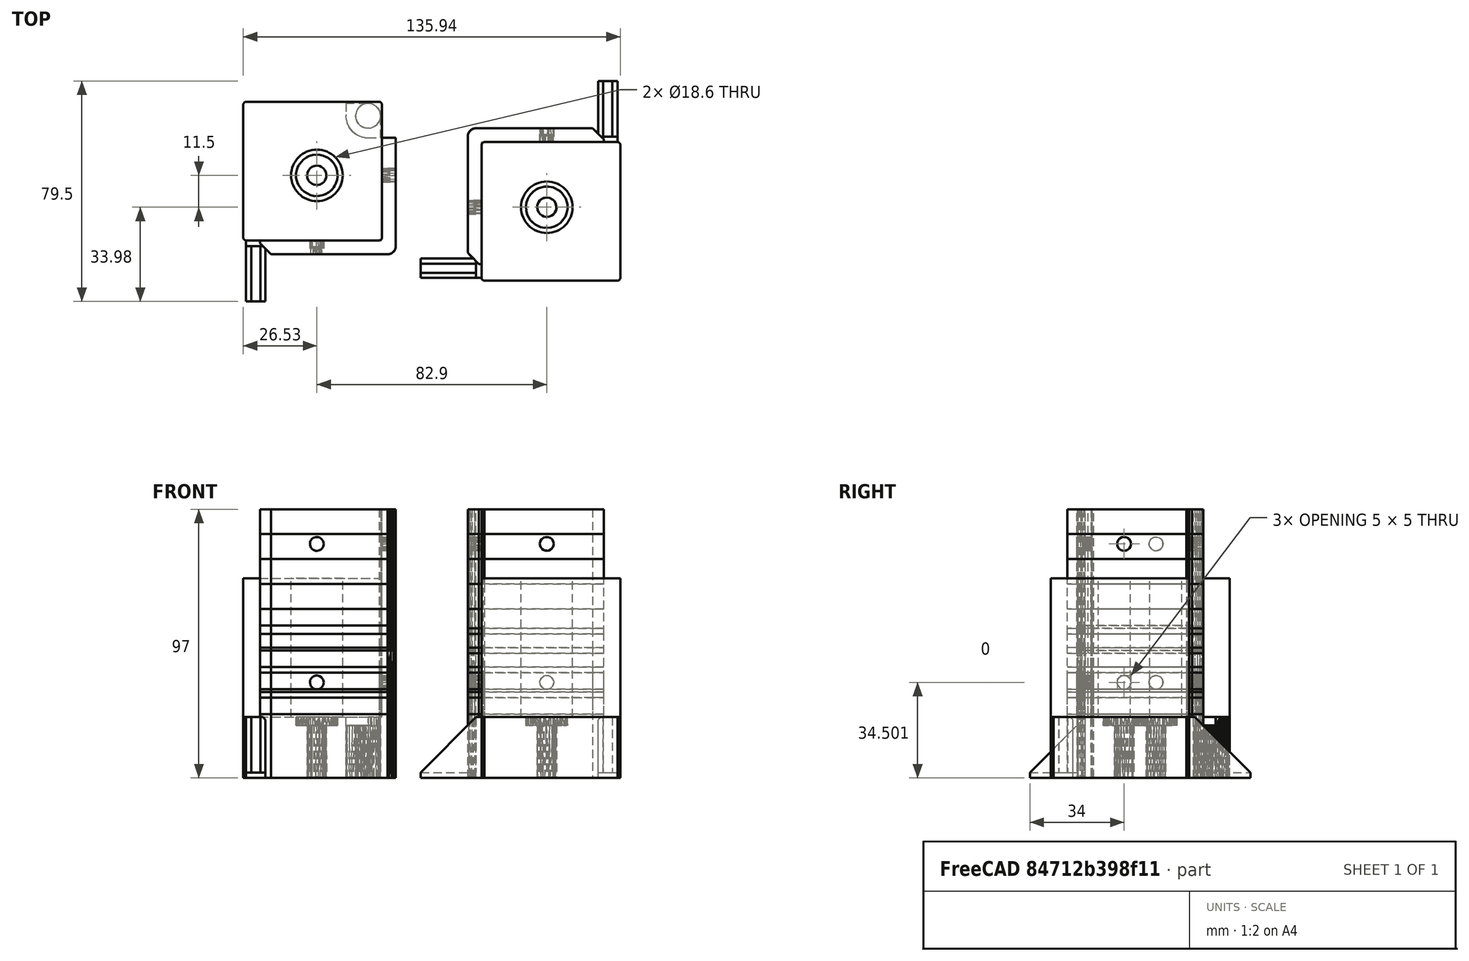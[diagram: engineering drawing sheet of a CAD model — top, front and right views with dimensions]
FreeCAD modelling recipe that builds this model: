
FCSTD DOCUMENT  (FreeCAD 0.18R14555 (Git shallow))
Label: top-holder-50mm-extend
License: All rights reserved
LicenseURL: http://en.wikipedia.org/wiki/All_rights_reserved
objects: Part::Feature×22, Part::Box×7, Part::Cut×5, Part::MultiCommon×4, Part::Cylinder×2, App::DocumentObjectGroup×2, Part::Fillet×1
note: 41 computed .brp shape members not serialized (recipe doc carries the construction recipe); baked Part::Feature solids carry a one-line shape summary decoded from their .brp

FEATURE [Part::Feature] top_corner_handle001001_solid  label="top_corner_handle002 (Solid)"
  Placement = pos=(30.38,0.35,0) rot=(0,0,1;0rad)
  shape: bbox 55 x 72 x 47 mm, 346 faces (baked)
FEATURE [Part::Feature] blain_top_corner001001_solid  label="blain_top_corner002 (Solid)"
  Placement = pos=(52.59,0.98,0) rot=(0,0,1;0rad)
  shape: bbox 72 x 72 x 47 mm, 277 faces (baked)
FEATURE [Part::Box] Box  label="Cube"
  AttacherType = Attacher::AttachEngine3D
  Height = 27
  Length = 22
  Placement = pos=(-5.49,-35.73,2) rot=(0,0,1;0rad)
  Width = 3.3
FEATURE [Part::Box] Box001  label="Cube001"
  AttacherType = Attacher::AttachEngine3D
  Height = 27
  Length = 3.3
  Placement = pos=(-64.58,-48.08,2) rot=(0,0,1;0rad)
  Width = 22
FEATURE [Part::Box] Box002  label="Cube002"
  AttacherType = Attacher::AttachEngine3D
  Height = 27
  Length = 3.3
  Placement = pos=(62.36,13.42,2) rot=(0,0,1;0rad)
  Width = 22
FEATURE [Part::Cut] Cut
  Base = -> top_corner_handle001001_solid
  Tool = -> Box001
FEATURE [Part::Cut] Cut001
  Base = -> blain_top_corner001001_solid
  Tool = -> Box002
FEATURE [Part::Cut] Cut002
  Base = -> Cut001
  Tool = -> Box
FEATURE [Part::Feature] Fillet001
  shape: bbox 50 x 50 x 50 mm, 9 faces (baked)
FEATURE [Part::Feature] Fillet002
  Placement = pos=(-85.94,14.5,0) rot=(0,0,1;0rad)
  shape: bbox 50 x 50 x 50 mm, 9 faces (baked)
FEATURE [Part::Feature] Cut002001  label="Cut003"
  shape: bbox 72 x 72 x 47 mm, 288 faces (baked)
FEATURE [Part::Feature] Cut002002  label="Cut004"
  shape: bbox 55 x 72 x 47 mm, 348 faces (baked)
FEATURE [Part::Box] Box003  label="Cube003"
  AttacherType = Attacher::AttachEngine3D
  Height = 9
  Length = 60
  Placement = pos=(10,-42,29) rot=(0,0,1;0rad)
  Width = 60
FEATURE [Part::Box] Box004  label="Cube004"
  AttacherType = Attacher::AttachEngine3D
  Height = 9
  Length = 60
  Placement = pos=(-70,-30,23) rot=(0,0,1;0rad)
  Width = 60
FEATURE [Part::Box] Box005  label="Cube005"
  AttacherType = Attacher::AttachEngine3D
  Height = 9
  Length = 60
  Placement = pos=(10,-42,23) rot=(0,0,1;0rad)
  Width = 60
FEATURE [Part::Feature] Cut002003  label="Cut005"
  shape: bbox 72 x 72 x 47 mm, 288 faces (baked)
FEATURE [Part::MultiCommon] Common
  Shapes = -> [Cut002001,Box005]
FEATURE [Part::MultiCommon] Common001
  Shapes = -> [Box003,Cut002003]
FEATURE [Part::Box] Box007  label="Cube007"
  AttacherType = Attacher::AttachEngine3D
  Height = 9
  Length = 60
  Placement = pos=(-70,-30,29) rot=(0,0,1;0rad)
  Width = 60
FEATURE [Part::Feature] Cut002004  label="Cut006"
  shape: bbox 55 x 72 x 47 mm, 348 faces (baked)
FEATURE [Part::MultiCommon] Common002
  Shapes = -> [Cut002002,Box007]
FEATURE [Part::MultiCommon] Common003
  Shapes = -> [Box004,Cut002004]
FEATURE [Part::Feature] Common003001  label="Common004"
  Placement = pos=(0,0,65) rot=(0,0,1;0rad)
  shape: bbox 49 x 42 x 9 mm, 29 faces (baked)
FEATURE [Part::Feature] Common003002  label="Common005"
  Placement = pos=(0,0,65) rot=(0,0,1;0rad)
  shape: bbox 49 x 49 x 9 mm, 32 faces (baked)
FEATURE [Part::Feature] Common001001  label="Common006"
  Placement = pos=(0,0,50) rot=(0,0,1;0rad)
  shape: bbox 49 x 49 x 9 mm, 121 faces (baked)
FEATURE [Part::Feature] Common002001  label="Common007"
  Placement = pos=(0,0,50) rot=(0,0,1;0rad)
  shape: bbox 49 x 42 x 9 mm, 114 faces (baked)
FEATURE [Part::Feature] Common003003  label="Common008"
  Placement = pos=(0,0,47) rot=(0,0,1;0rad)
  shape: bbox 49 x 49 x 9 mm, 32 faces (baked)
FEATURE [Part::Feature] Common003004  label="Common009"
  Placement = pos=(0,0,38) rot=(0,0,1;0rad)
  shape: bbox 49 x 49 x 9 mm, 32 faces (baked)
FEATURE [Part::Feature] Common003005  label="Common010"
  Placement = pos=(0,0,29) rot=(0,0,1;0rad)
  shape: bbox 49 x 49 x 9 mm, 32 faces (baked)
FEATURE [Part::Feature] Common003006  label="Common011"
  Placement = pos=(0,0,22) rot=(0,0,1;0rad)
  shape: bbox 49 x 49 x 9 mm, 32 faces (baked)
FEATURE [Part::Feature] Common003007  label="Common012"
  Placement = pos=(0,0,8) rot=(0,0,1;0rad)
  shape: bbox 49 x 49 x 9 mm, 32 faces (baked)
FEATURE [Part::Feature] Common003008  label="Common013"
  Placement = pos=(0,0,47) rot=(0,0,1;0rad)
  shape: bbox 49 x 42 x 9 mm, 29 faces (baked)
FEATURE [Part::Feature] Common003009  label="Common014"
  Placement = pos=(0,0,29) rot=(0,0,1;0rad)
  shape: bbox 49 x 42 x 9 mm, 29 faces (baked)
FEATURE [Part::Feature] Common003010  label="Common015"
  Placement = pos=(0,0,38) rot=(0,0,1;0rad)
  shape: bbox 49 x 42 x 9 mm, 29 faces (baked)
FEATURE [Part::Feature] Common003011  label="Common016"
  Placement = pos=(0,0,23) rot=(0,0,1;0rad)
  shape: bbox 49 x 42 x 9 mm, 29 faces (baked)
FEATURE [Part::Feature] Common003012  label="Common017"
  Placement = pos=(0,0,8) rot=(0,0,1;0rad)
  shape: bbox 49 x 42 x 9 mm, 29 faces (baked)
FEATURE [Part::Cylinder] Cylinder
  Angle = 360
  AttacherType = Attacher::AttachEngine3D
  Height = 66
  Placement = pos=(-40.9,-0.6,22) rot=(0,0,1;0rad)
  Radius = 9.3
FEATURE [Part::Cylinder] Cylinder001
  Angle = 360
  AttacherType = Attacher::AttachEngine3D
  Height = 63
  Placement = pos=(42,-12.1,22) rot=(0,0,1;0rad)
  Radius = 9.3
FEATURE [Part::Fillet] Fillet
  Base = -> Fillet002
  Edges = 1 edges r=1: [Edge3]
FEATURE [Part::Cut] Cut002005
  Base = -> Fillet
  Tool = -> Cylinder
FEATURE [Part::Cut] Cut002006
  Base = -> Fillet001
  Tool = -> Cylinder001
FEATURE [App::DocumentObjectGroup] Group  label="corner-1"
  Group = -> [Cut002,Common003007,Common003006,Common003005,Common003004,Common003003,Common001001,Common003002,Cut002006]
FEATURE [App::DocumentObjectGroup] Group001  label="corner-2"
  Group = -> [Cut002005,Common003012,Common003011,Common003010,Common003009,Common003008,Common002001,Common003001,Cut]
